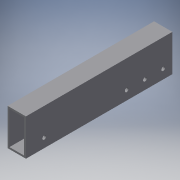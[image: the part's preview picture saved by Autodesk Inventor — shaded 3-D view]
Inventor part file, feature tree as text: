
AUTODESK INVENTOR PART (.ipt)
format: ipt  version: 2018 (Build 220112000, 112)  size: 141,824 bytes
history: native  units: in
note: dims shown in document units (in); Inventor stores cm internally (conversion verified against a paired STEP export)
features: extrude x4, sketch x4
ambient origin geometry x8: Origin, YZ Plane, XZ Plane, XY Plane, X Axis, Y Axis, Z Axis, Center Point
bodies: Solid1 (feature_tree)
feature tree (8):
  extrude  "Extrusion1"  Depth=1.0in
  extrude  "Extrusion2"  Depth=0.1in
  extrude  "Extrusion3"  Depth=0.1in
  extrude  "Extrusion4"  Depth=1.0in
  sketch  "Sketch1"  dims[d0=2.0in d1=1.0in]
  sketch  "Sketch2"  dims[d2=0.1in d3=0.1in]
  sketch  "Sketch3"  dims[d4=0.1in d5=0.1in]
  sketch  "Sketch4"  dims[d6=8.0in d7=0.0in d8=0.2031in d10=0.2031in d11=0.2031in d12=0.5in d13=0.5in d14=0.5in d16=0.5in d18=1.5in d21=1.0in d22=8.0in d23=0.0in d24=0.2031in d25=2.556in d26=0.5in d27=8.0in d28=0.0in d29=1.125in d31=1.0in d32=1.0in d33=1.0in d34=0.0in]
